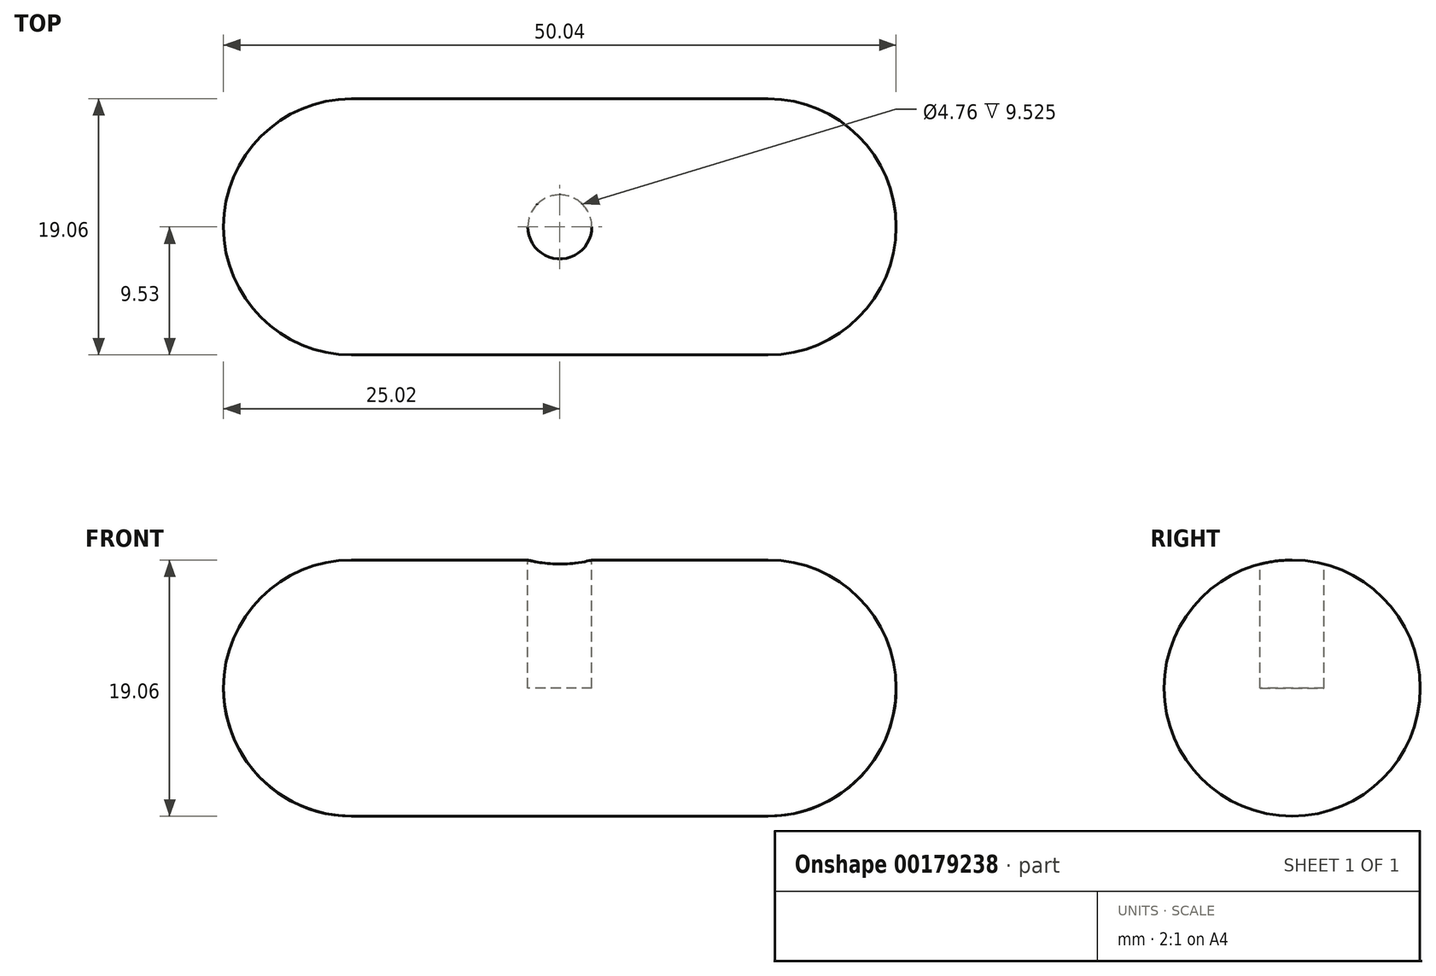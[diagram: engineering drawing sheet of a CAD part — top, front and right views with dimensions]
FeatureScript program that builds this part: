
annotation { "Feature Type Name" : "Feature", "Feature Type Description" : "" }
export const myFeature = defineFeature(function(context is Context, id is Id, definition is map)
    precondition{}
    {
        {
            var Q0;
            Q0=qCreatedBy(makeId("Right.planeOp"),FACE);
            var sketch = newSketch(context, id + "F0", { "sketchPlane" : qUnion([Q0])});
            skCircle(sketch, "E0", {"center": v(0, 0) * mm, "radius": 9.53 * mm});
            skPoint(sketch, "E1", {"position": v(0, 9.53) * mm});
            skSolve(sketch);
        }
        {
            var Q0;
            Q0=makeQuery(id+"F0.imprint","IMPRINT",FACE,{"disambiguationData":[TD([[makeQuery(id+"F0.imprint","IMPRINT",EDGE,{"derivedFrom":sQuery(id+"F0.wireOp",EDGE,"E0")}),1.0]])]});
            extrude(context, id + "F1", {"entities" : qUnion([Q0]), "endBound" : BoundingType.SYMMETRIC, "depth" : 50.04 * mm});
        }
        {
            var Q0;
            Q0=makeQuery(id+"F1.opExtrude","CAP_EDGE",EDGE,{"disambiguationData":[OSD([sQuery(id+"F0.wireOp",EDGE,"E0")])],"isStart":true});
            var Q1;
            Q1=makeQuery(id+"F1.opExtrude","CAP_EDGE",EDGE,{"disambiguationData":[OSD([sQuery(id+"F0.wireOp",EDGE,"E0")])],"isStart":false});
            fillet(context, id + "F2", {"entities" : qUnion([Q0, Q1]), "radius" : 9.52 * mm, "tangentPropagation" : true, "allowEdgeOverflow" : false});
        }
        {
            var Q0;
            Q0=sQuery(id+"F0.wireOp",VERTEX,"E1");
            var Q1;
            Q1=qCreatedBy(makeId("Top.planeOp"),FACE);
            cPlane(context, id + "F3", {"entities" : qUnion([Q0, Q1]), "cplaneType" : CPlaneType.PLANE_POINT, "offset" : 25.4 * mm, "width" : 152.4 * mm, "height" : 152.4 * mm});
        }
        {
            var Q0;
            Q0=qCreatedBy(id+"F3.planeOp",FACE);
            var sketch = newSketch(context, id + "F4", { "sketchPlane" : qUnion([Q0])});
            skCircle(sketch, "E2", {"center": v(0, 0) * mm, "radius": 2.38 * mm});
            skSolve(sketch);
        }
        {
            var Q0;
            Q0=makeQuery(id+"F4.imprint","IMPRINT",FACE,{"disambiguationData":[TD([[makeQuery(id+"F4.imprint","IMPRINT",EDGE,{"derivedFrom":sQuery(id+"F4.wireOp",EDGE,"E2")}),1.0]])]});
            extrude(context, id + "F5", {"entities" : qUnion([Q0]), "operationType" : NewBodyOperationType.REMOVE, "oppositeDirection" : true, "depth" : 9.52 * mm});
        }
    });
